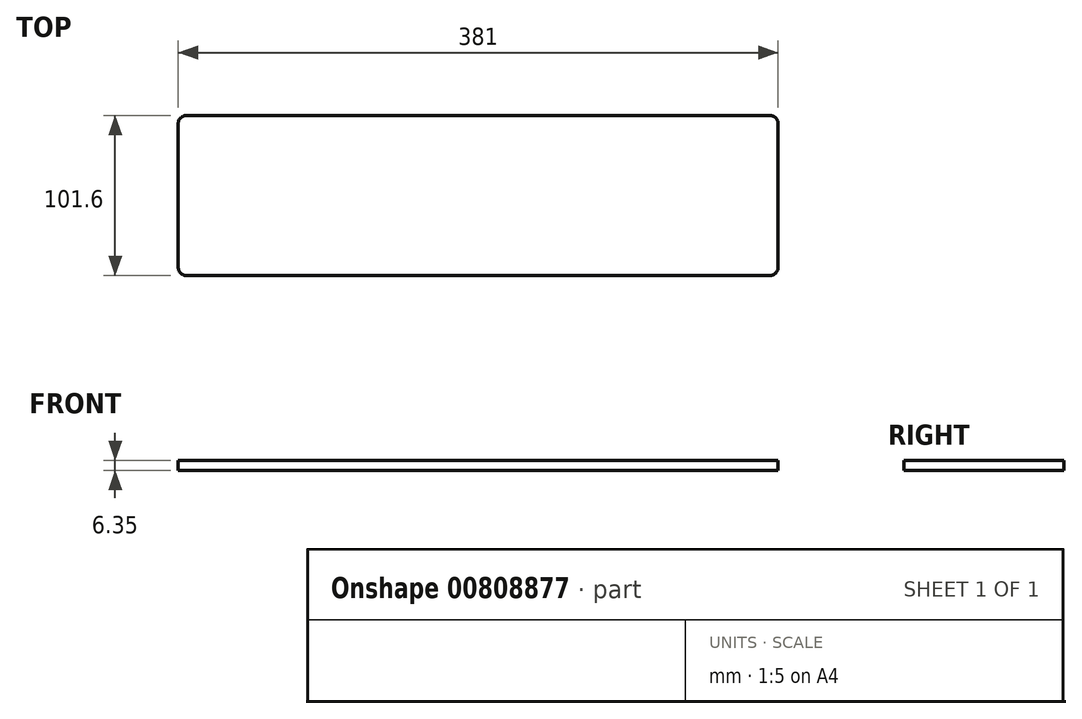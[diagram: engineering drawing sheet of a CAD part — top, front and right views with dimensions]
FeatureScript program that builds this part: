
annotation { "Feature Type Name" : "Feature", "Feature Type Description" : "" }
export const myFeature = defineFeature(function(context is Context, id is Id, definition is map)
    precondition{}
    {
        {
            var Q0;
            Q0=qCreatedBy(makeId("Top.planeOp"),FACE);
            var sketch = newSketch(context, id + "F0", { "sketchPlane" : qUnion([Q0])});
            skPoint(sketch, "E0.middle", {"position": v(0, 0) * mm});
            skLineSegment(sketch, "E1.bottom", {"start": v(190.5, -50.8) * mm, "end": v(-190.5, -50.8) * mm});
            skLineSegment(sketch, "E1.top", {"start": v(190.5, 50.8) * mm, "end": v(-190.5, 50.8) * mm});
            skLineSegment(sketch, "E1.left", {"start": v(190.5, -50.8) * mm, "end": v(190.5, 50.8) * mm});
            skLineSegment(sketch, "E1.right", {"start": v(-190.5, -50.8) * mm, "end": v(-190.5, 50.8) * mm});
            skSolve(sketch);
        }
        {
            var Q0;
            Q0=makeQuery(id+"F0.imprint","IMPRINT",FACE,{"disambiguationData":[TD([[makeQuery(id+"F0.imprint","IMPRINT",EDGE,{"derivedFrom":sQuery(id+"F0.wireOp",EDGE,"E1.bottom")}),-1.0]])]});
            extrude(context, id + "F1", {"entities" : qUnion([Q0]), "depth" : 6.35 * mm, "offsetDistance" : 25.4 * mm});
        }
        {
            var Q0;
            Q0=makeQuery(id+"F1.opExtrude","SWEPT_EDGE",EDGE,{"disambiguationData":[OSD([sQuery(id+"F0.wireOp",EDGE,"E1.top"),sQuery(id+"F0.wireOp",EDGE,"E1.right")])]});
            var Q1;
            Q1=makeQuery(id+"F1.opExtrude","SWEPT_EDGE",EDGE,{"disambiguationData":[OSD([sQuery(id+"F0.wireOp",EDGE,"E1.top"),sQuery(id+"F0.wireOp",EDGE,"E1.left")])]});
            var Q2;
            Q2=makeQuery(id+"F1.opExtrude","SWEPT_EDGE",EDGE,{"disambiguationData":[OSD([sQuery(id+"F0.wireOp",EDGE,"E1.bottom"),sQuery(id+"F0.wireOp",EDGE,"E1.left")])]});
            var Q3;
            Q3=makeQuery(id+"F1.opExtrude","SWEPT_EDGE",EDGE,{"disambiguationData":[OSD([sQuery(id+"F0.wireOp",EDGE,"E1.bottom"),sQuery(id+"F0.wireOp",EDGE,"E1.right")])]});
            fillet(context, id + "F2", {"entities" : qUnion([Q0, Q1, Q2, Q3]), "radius" : 5.08 * mm, "tangentPropagation" : true, "allowEdgeOverflow" : false});
        }
    });
